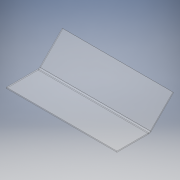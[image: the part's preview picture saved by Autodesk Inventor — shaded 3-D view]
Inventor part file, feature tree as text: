
AUTODESK INVENTOR PART (.ipt)
format: ipt  version: 2018 (Build 220112000, 112)  size: 146,944 bytes
history: native  units: mm
features: sheet_metal_op x4, sketch x2, other x2
ambient origin geometry x8: Origin, YZ Plane, XZ Plane, XY Plane, X Axis, Y Axis, Z Axis, Center Point
bodies: Solid1 (feature_tree)
feature tree (8):
  sheet_metal_op  "Face1"
  sheet_metal_op  "Flange1"
  sketch  "Sketch1"  dims[d0=1000.0mm]
  other  "Plate1"
  sketch  "Sketch2"  dims[d1=300.0mm d2=10.0mm d3=10.0mm d4=5.0mm d5=20.0mm d6=10.0mm d7=300.0mm d8=45.0deg d9=20.0mm d10=40.0mm d11=10.0mm d12=10.0mm]
  other  "Plate2"
  sheet_metal_op  "Bend1"
  sheet_metal_op  "Corner1"
